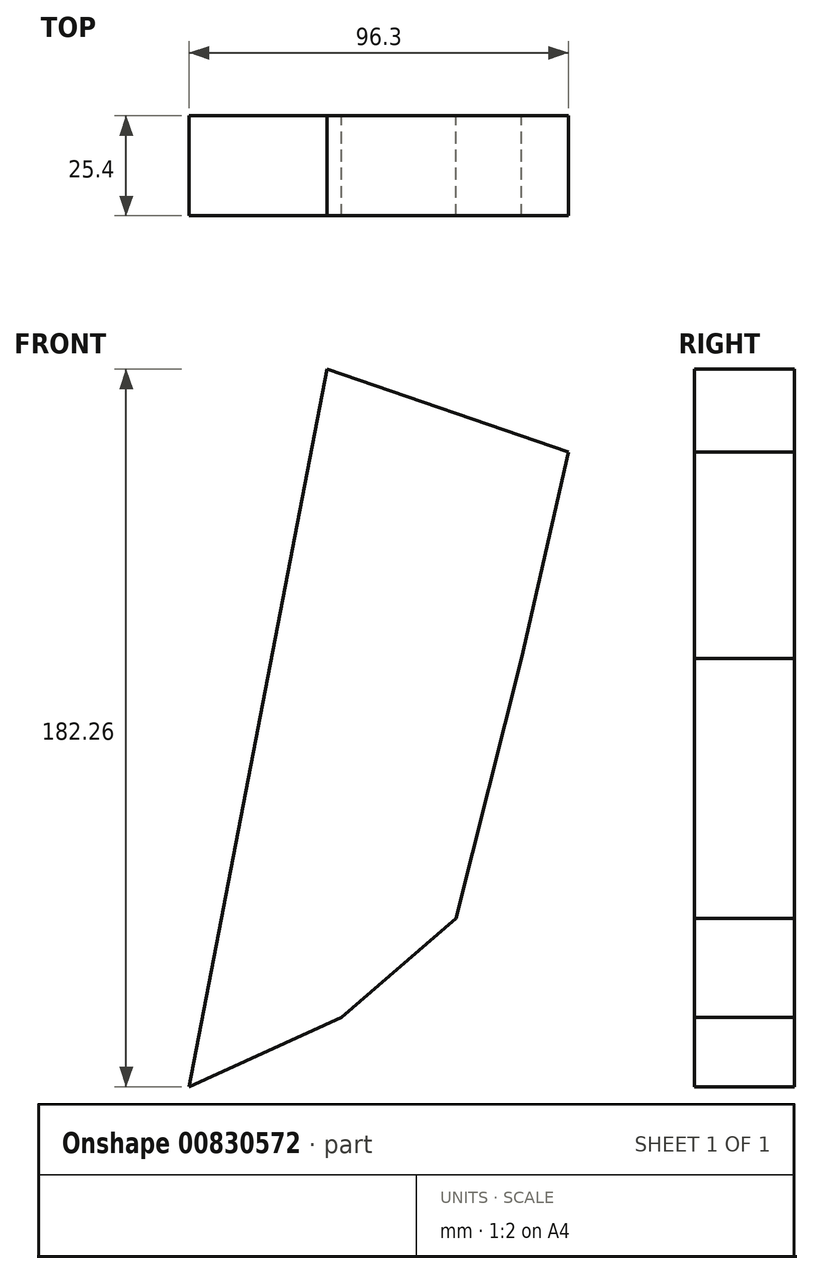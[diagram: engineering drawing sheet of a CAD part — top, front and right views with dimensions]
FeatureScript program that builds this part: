
annotation { "Feature Type Name" : "Feature", "Feature Type Description" : "" }
export const myFeature = defineFeature(function(context is Context, id is Id, definition is map)
    precondition{}
    {
        {
            var Q0;
            Q0=qCreatedBy(makeId("Front.planeOp"),FACE);
            var sketch = newSketch(context, id + "F0", { "sketchPlane" : qUnion([Q0])});
            skLineSegment(sketch, "E0", {"start": v(6.19, 111.81) * mm, "end": v(-28.78, -70.45) * mm});
            skLineSegment(sketch, "E1", {"start": v(6.19, 111.81) * mm, "end": v(67.52, 90.78) * mm});
            skLineSegment(sketch, "E2", {"start": v(67.52, 90.78) * mm, "end": v(55.68, 38.4) * mm});
            skLineSegment(sketch, "E3", {"start": v(55.68, 38.4) * mm, "end": v(39, -27.75) * mm});
            skLineSegment(sketch, "E4", {"start": v(39, -27.75) * mm, "end": v(9.95, -52.81) * mm});
            skLineSegment(sketch, "E5", {"start": v(9.95, -52.81) * mm, "end": v(-28.78, -70.45) * mm});
            skSolve(sketch);
        }
        {
            var Q0;
            Q0=makeQuery(id+"F0.imprint","IMPRINT",FACE,{"disambiguationData":[TD([[makeQuery(id+"F0.imprint","IMPRINT",EDGE,{"derivedFrom":sQuery(id+"F0.wireOp",EDGE,"E0")}),1.0]])]});
            extrude(context, id + "F1", {"entities" : qUnion([Q0]), "depth" : 25.4 * mm, "offsetDistance" : 25.4 * mm});
        }
    });
